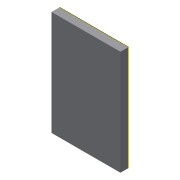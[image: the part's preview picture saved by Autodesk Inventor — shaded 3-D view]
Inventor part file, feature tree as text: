
AUTODESK INVENTOR PART (.ipt)
format: ipt  version: 2014 (Build 180170000, 170)  size: 82,432 bytes
history: native  units: mm
features: sketch x2, other x2, extrude x1
ambient origin geometry x8: Origin, YZ Plane, XZ Plane, XY Plane, X Axis, Y Axis, Z Axis, Center Point
bodies: Volumenkörper1 (feature_tree)
feature tree (5):
  extrude  "Extrusion1"  [1 undecoded]
  sketch  "Skizze5"
  other  "Arbeitspunkt7"
  other  "Arbeitspunkt8"
  sketch  "Skizze1"  dims[d0=1.5mm d1=0.0mm]
note: 1 required parameter value undecoded (feature->parameter linkage not recoverable at this tier; creation-order binding heuristic only, values carry confidence <= 0.55)
